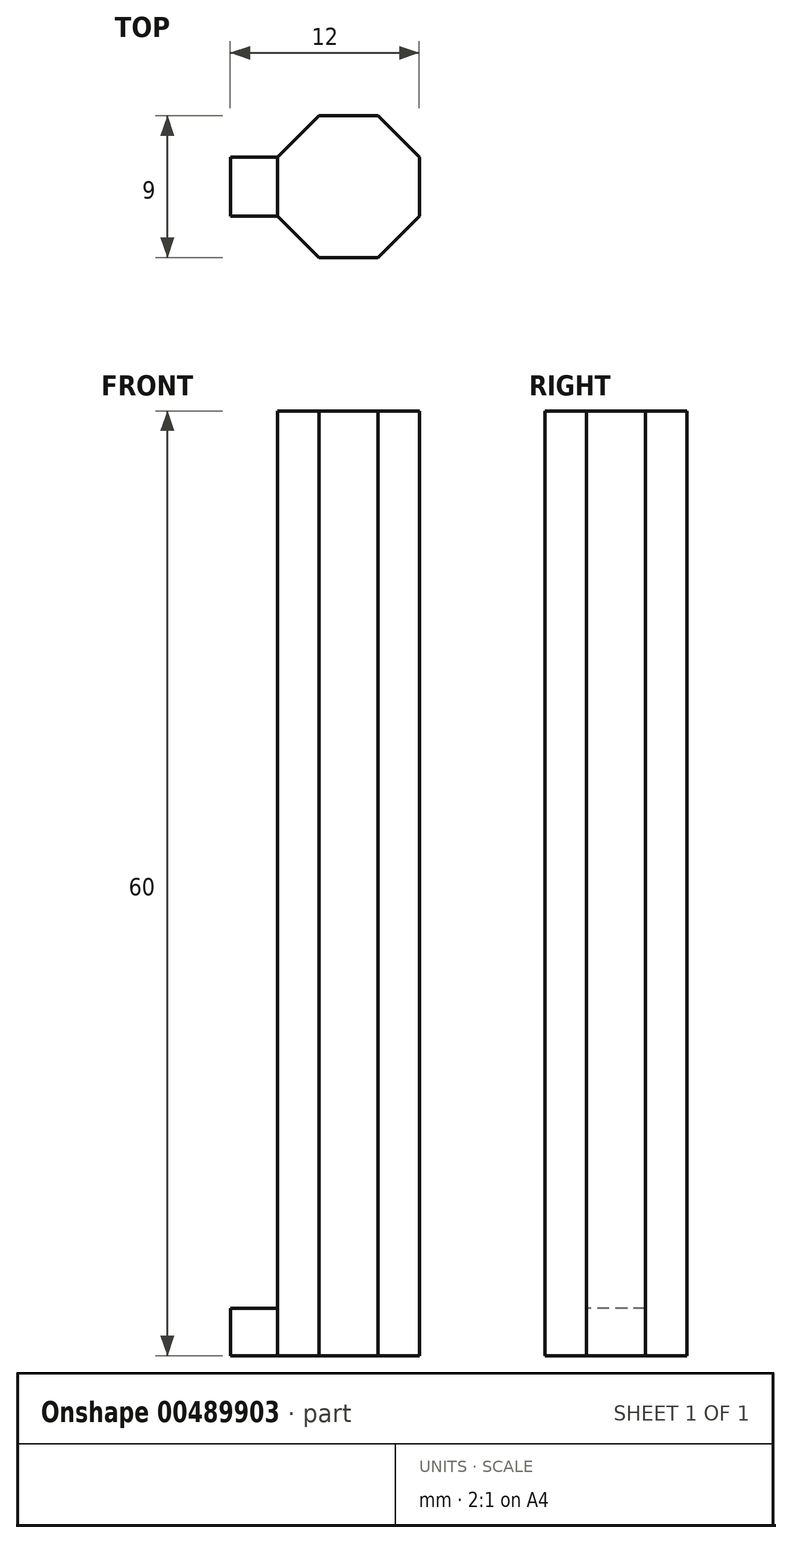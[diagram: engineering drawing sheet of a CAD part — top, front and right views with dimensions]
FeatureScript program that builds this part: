
annotation { "Feature Type Name" : "Feature", "Feature Type Description" : "" }
export const myFeature = defineFeature(function(context is Context, id is Id, definition is map)
    precondition{}
    {
        {
            var Q0;
            Q0=qCreatedBy(makeId("Top.planeOp"),FACE);
            var sketch = newSketch(context, id + "F0", { "sketchPlane" : qUnion([Q0])});
            skCircle(sketch, "E0.cCircle", {"center": v(-61.37, 30.24) * mm, "radius": 4.5 * mm, "construction": true});
            skLineSegment(sketch, "E0.0", {"start": v(-56.87, 28.37) * mm, "end": v(-59.5, 25.74) * mm});
            skLineSegment(sketch, "E0.1", {"start": v(-59.5, 25.74) * mm, "end": v(-63.23, 25.74) * mm});
            skLineSegment(sketch, "E0.2", {"start": v(-63.23, 25.74) * mm, "end": v(-65.87, 28.37) * mm});
            skLineSegment(sketch, "E0.3", {"start": v(-65.87, 28.37) * mm, "end": v(-65.87, 32.1) * mm});
            skLineSegment(sketch, "E0.4", {"start": v(-65.87, 32.1) * mm, "end": v(-63.23, 34.74) * mm});
            skLineSegment(sketch, "E0.5", {"start": v(-63.23, 34.74) * mm, "end": v(-59.5, 34.74) * mm});
            skLineSegment(sketch, "E0.6", {"start": v(-59.5, 34.74) * mm, "end": v(-56.87, 32.1) * mm});
            skLineSegment(sketch, "E0.7", {"start": v(-56.87, 32.1) * mm, "end": v(-56.87, 28.37) * mm});
            skPoint(sketch, "E0.0.midPoint", {"position": v(-58.18, 27.06) * mm});
            skLineSegment(sketch, "E1", {"start": v(-61.37, 34.74) * mm, "end": v(-61.37, 25.74) * mm, "construction": true});
            skSolve(sketch);
        }
        {
            var Q0;
            Q0=makeQuery(id+"F0.imprint","IMPRINT",FACE,{"disambiguationData":[TD([[makeQuery(id+"F0.imprint","IMPRINT",EDGE,{"derivedFrom":sQuery(id+"F0.wireOp",EDGE,"E0.0")}),-1.0]])]});
            extrude(context, id + "F1", {"entities" : qUnion([Q0]), "depth" : 60 * mm});
        }
        {
            var Q0;
            Q0=makeQuery(id+"F1.opExtrude","SWEPT_FACE",FACE,{"disambiguationData":[OSD([sQuery(id+"F0.wireOp",EDGE,"E0.3")])]});
            var sketch = newSketch(context, id + "F2", { "sketchPlane" : qUnion([Q0])});
            skLineSegment(sketch, "E2.bottom", {"start": v(-32.1, 0) * mm, "end": v(-28.37, 0) * mm});
            skLineSegment(sketch, "E2.top", {"start": v(-32.1, 3) * mm, "end": v(-28.37, 3) * mm});
            skLineSegment(sketch, "E2.left", {"start": v(-32.1, 0) * mm, "end": v(-32.1, 3) * mm});
            skLineSegment(sketch, "E2.right", {"start": v(-28.37, 0) * mm, "end": v(-28.37, 3) * mm});
            skSolve(sketch);
        }
        {
            var Q0;
            Q0=makeQuery(id+"F2.imprint","IMPRINT",FACE,{"disambiguationData":[TD([[makeQuery(id+"F2.imprint","IMPRINT",EDGE,{"derivedFrom":sQuery(id+"F2.wireOp",EDGE,"E2.bottom")}),-1.0]])]});
            extrude(context, id + "F3", {"entities" : qUnion([Q0]), "operationType" : NewBodyOperationType.ADD, "depth" : 3 * mm});
        }
    });
